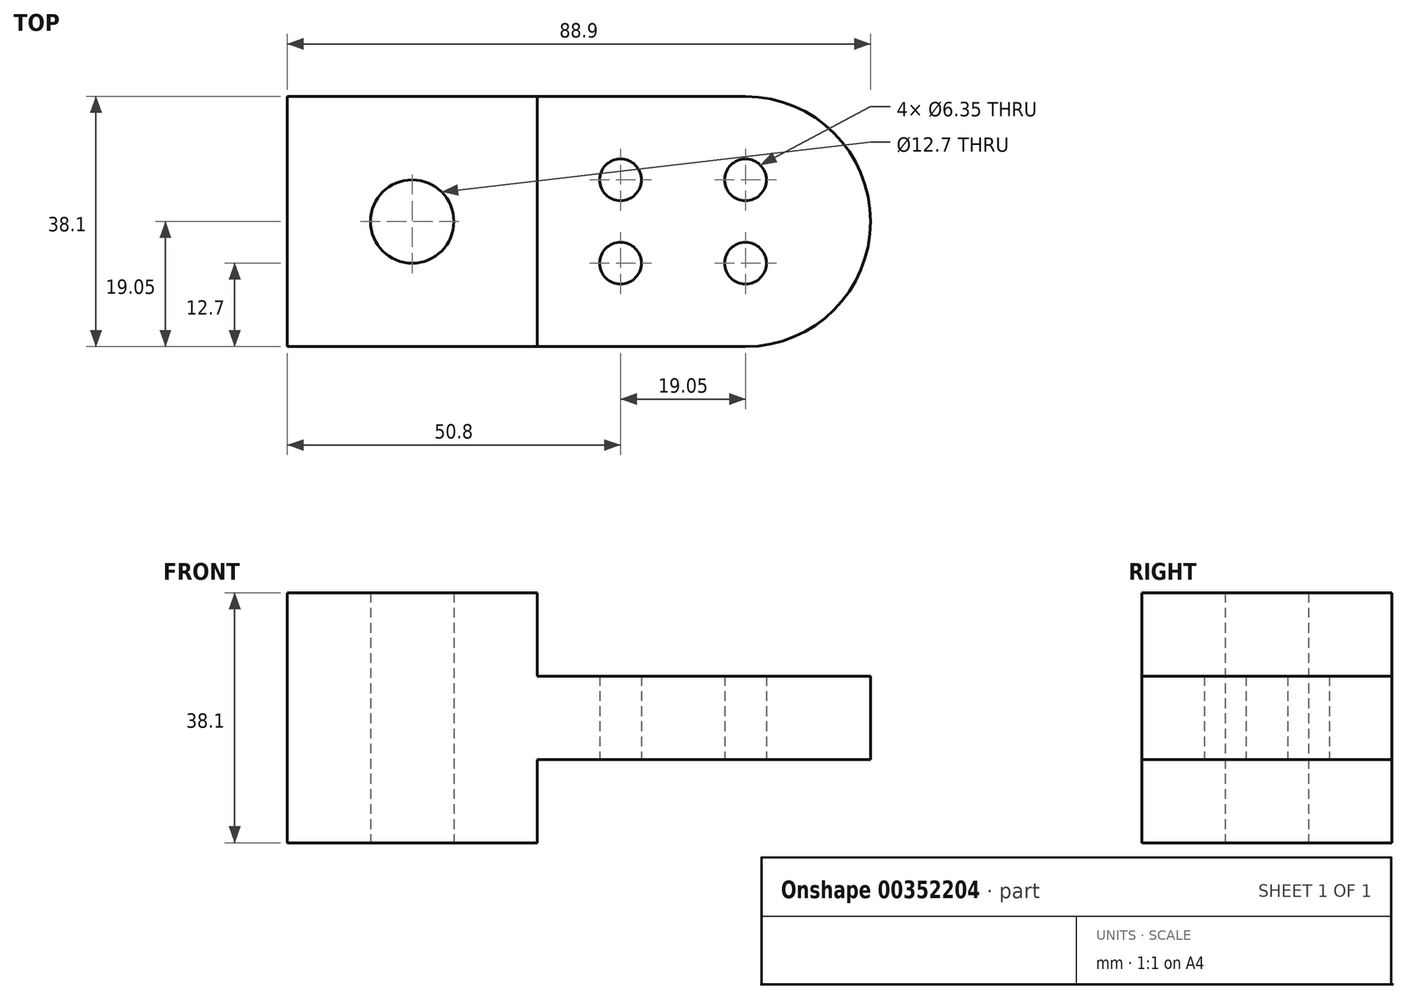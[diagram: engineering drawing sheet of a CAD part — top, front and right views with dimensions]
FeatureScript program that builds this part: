
annotation { "Feature Type Name" : "Feature", "Feature Type Description" : "" }
export const myFeature = defineFeature(function(context is Context, id is Id, definition is map)
    precondition{}
    {
        {
            var Q0;
            Q0=qCreatedBy(makeId("Top.planeOp"),FACE);
            var sketch = newSketch(context, id + "F0", { "sketchPlane" : qUnion([Q0])});
            skLineSegment(sketch, "E0", {"start": v(0, 0) * mm, "end": v(0, 38.1) * mm});
            skLineSegment(sketch, "E1", {"start": v(0, 38.1) * mm, "end": v(38.1, 38.1) * mm});
            skLineSegment(sketch, "E2", {"start": v(38.1, 38.1) * mm, "end": v(38.1, 0) * mm});
            skLineSegment(sketch, "E3", {"start": v(38.1, 0) * mm, "end": v(0, 0) * mm});
            skLineSegment(sketch, "E4", {"start": v(38.1, 38.1) * mm, "end": v(69.85, 38.1) * mm});
            skLineSegment(sketch, "E5", {"start": v(38.1, 0) * mm, "end": v(69.85, 0) * mm});
            skArc(sketch, "E6", {"start": v(69.85, 38.1) * mm, "mid": v(88.9, 19.05) * mm, "end": v(69.85, 0) * mm});
            skCircle(sketch, "E7", {"center": v(19.05, 19.05) * mm, "radius": 6.35 * mm});
            skCircle(sketch, "E8", {"center": v(50.8, 25.4) * mm, "radius": 3.18 * mm});
            skCircle(sketch, "E9", {"center": v(50.8, 12.7) * mm, "radius": 3.18 * mm});
            skCircle(sketch, "E10", {"center": v(69.85, 12.7) * mm, "radius": 3.18 * mm});
            skCircle(sketch, "E11", {"center": v(69.85, 25.4) * mm, "radius": 3.18 * mm});
            skLineSegment(sketch, "E12", {"start": v(69.85, 38.1) * mm, "end": v(69.85, 0) * mm, "construction": true});
            skSolve(sketch);
        }
        {
            var Q0;
            Q0=makeQuery(id+"F0.imprint","IMPRINT",FACE,{"disambiguationData":[TD([[makeQuery(id+"F0.imprint","IMPRINT",EDGE,{"derivedFrom":sQuery(id+"F0.wireOp",EDGE,"E0")}),-1.0]])]});
            extrude(context, id + "F1", {"entities" : qUnion([Q0]), "endBound" : BoundingType.SYMMETRIC, "depth" : 38.1 * mm});
        }
        {
            var Q0;
            Q0=makeQuery(id+"F0.imprint","IMPRINT",FACE,{"disambiguationData":[TD([[makeQuery(id+"F0.imprint","IMPRINT",EDGE,{"derivedFrom":sQuery(id+"F0.wireOp",EDGE,"E2")}),1.0]])]});
            extrude(context, id + "F2", {"entities" : qUnion([Q0]), "operationType" : NewBodyOperationType.ADD, "endBound" : BoundingType.SYMMETRIC, "depth" : 12.7 * mm});
        }
    });
